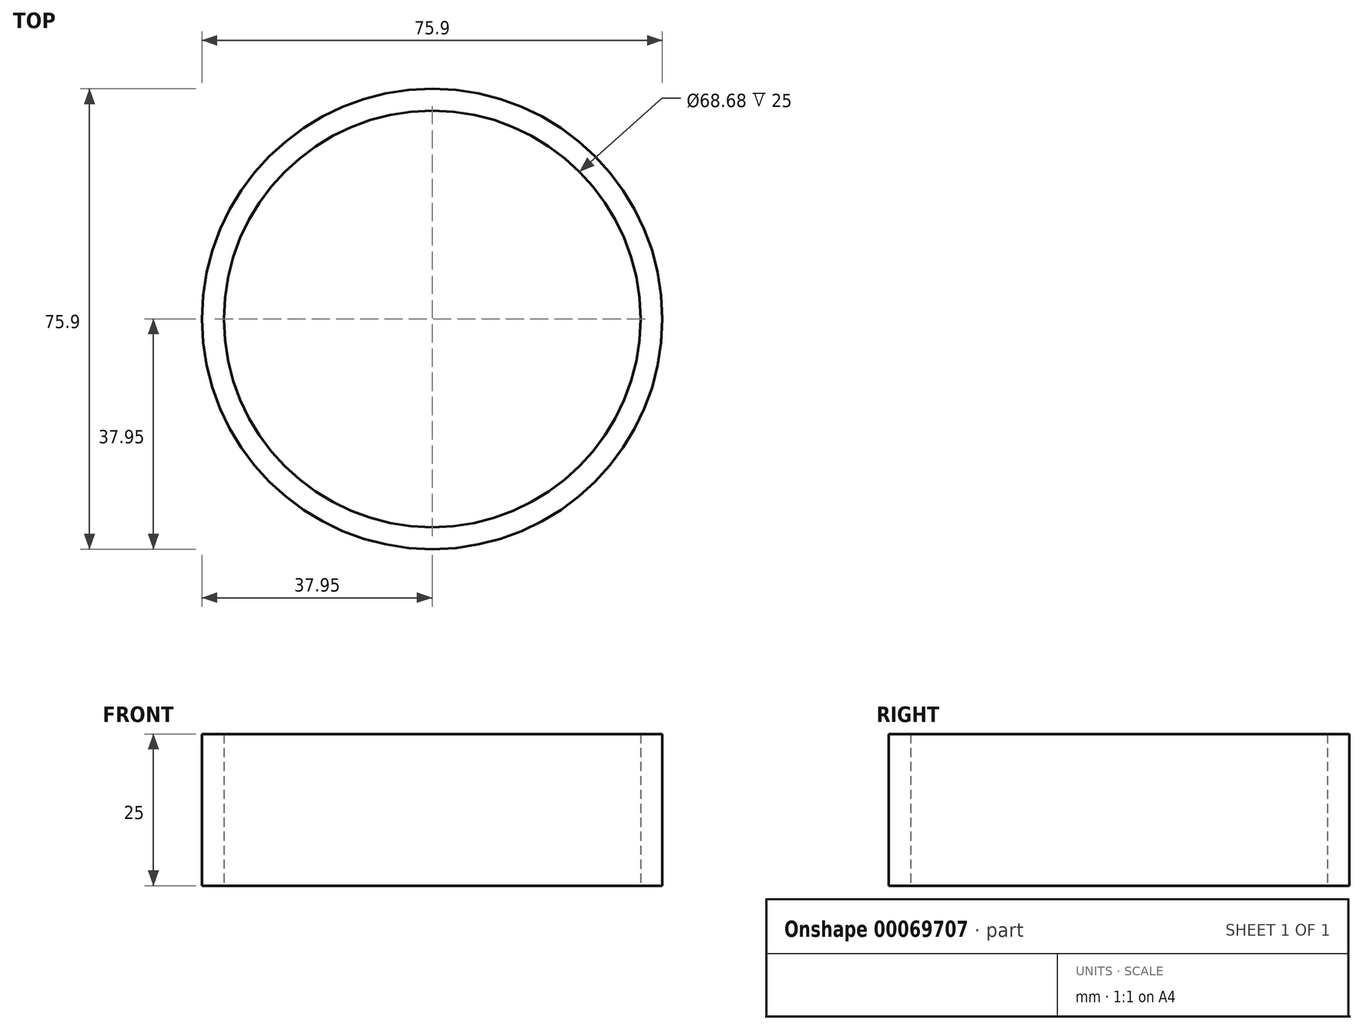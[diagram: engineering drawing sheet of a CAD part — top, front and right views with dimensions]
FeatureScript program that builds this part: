
annotation { "Feature Type Name" : "Feature", "Feature Type Description" : "" }
export const myFeature = defineFeature(function(context is Context, id is Id, definition is map)
    precondition{}
    {
        {
            var Q0;
            Q0=qCreatedBy(makeId("Top.planeOp"),FACE);
            var sketch = newSketch(context, id + "F0", { "sketchPlane" : qUnion([Q0])});
            skCircle(sketch, "E0", {"center": v(0, 0) * mm, "radius": 37.95 * mm});
            skSolve(sketch);
        }
        {
            var Q0;
            Q0=qCreatedBy(makeId("Top.planeOp"),FACE);
            var sketch = newSketch(context, id + "F1", { "sketchPlane" : qUnion([Q0])});
            skCircle(sketch, "E1", {"center": v(0, 0) * mm, "radius": 34.34 * mm});
            skSolve(sketch);
        }
        {
            var Q0;
            Q0=makeQuery(id+"F0.imprint","IMPRINT",FACE,{"disambiguationData":[TD([[makeQuery(id+"F0.imprint","IMPRINT",EDGE,{"derivedFrom":sQuery(id+"F0.wireOp",EDGE,"E0")}),1.0]])]});
            extrude(context, id + "F2", {"entities" : qUnion([Q0]), "depth" : 25 * mm});
        }
        {
            var Q0;
            Q0 = qSketchRegion(id + "F1", true);
            extrude(context, id + "F3", {"entities" : qUnion([Q0]), "operationType" : NewBodyOperationType.REMOVE, "depth" : 25 * mm});
        }
    });
